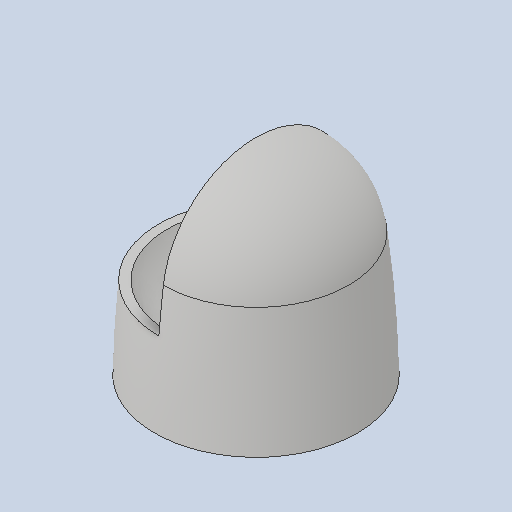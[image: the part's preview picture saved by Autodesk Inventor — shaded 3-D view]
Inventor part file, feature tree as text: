
AUTODESK INVENTOR PART (.ipt)
format: ipt  version: 2024.2 (Build 282272000, 272)  size: 142,848 bytes
history: native  units: mm
features: sketch x3, revolve x2, other x1, extrude x1
ambient origin geometry x8: Origin, YZ Plane, XZ Plane, XY Plane, X Axis, Y Axis, Z Axis, Center Point
bodies: Body1 (feature_tree)
feature tree (7):
  other  "Твердое тело1"
  revolve  "Вращение1"
  revolve  "Вращение2"
  extrude  "Выдавливание1"  Depth=100.0mm
  sketch  "Эскиз1"
  sketch  "Эскиз2"
  sketch  "Эскиз3"
